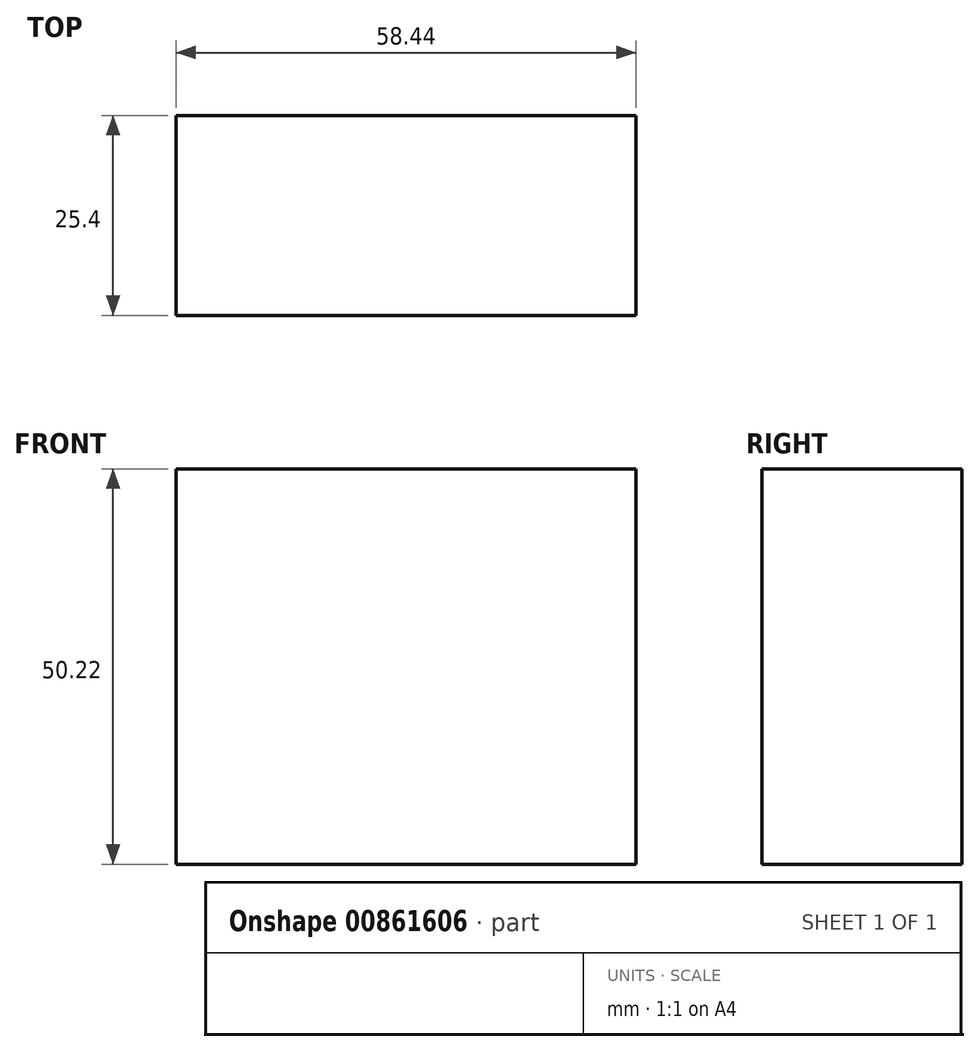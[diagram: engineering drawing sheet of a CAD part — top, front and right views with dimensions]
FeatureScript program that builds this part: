
annotation { "Feature Type Name" : "Feature", "Feature Type Description" : "" }
export const myFeature = defineFeature(function(context is Context, id is Id, definition is map)
    precondition{}
    {
        {
            var Q0;
            Q0=qCreatedBy(makeId("Front.planeOp"),FACE);
            var sketch = newSketch(context, id + "F0", { "sketchPlane" : qUnion([Q0])});
            skLineSegment(sketch, "E0.bottom", {"start": v(-29.22, 25.11) * mm, "end": v(29.22, 25.11) * mm});
            skLineSegment(sketch, "E0.top", {"start": v(-29.22, -25.11) * mm, "end": v(29.22, -25.11) * mm});
            skLineSegment(sketch, "E0.left", {"start": v(-29.22, 25.11) * mm, "end": v(-29.22, -25.11) * mm});
            skLineSegment(sketch, "E0.right", {"start": v(29.22, 25.11) * mm, "end": v(29.22, -25.11) * mm});
            skPoint(sketch, "E0.middle", {"position": v(0, 0) * mm});
            skSolve(sketch);
        }
        {
            var Q0;
            Q0=makeQuery(id+"F0.imprint","IMPRINT",FACE,{"disambiguationData":[TD([[makeQuery(id+"F0.imprint","IMPRINT",EDGE,{"derivedFrom":sQuery(id+"F0.wireOp",EDGE,"E0.bottom")}),-1.0]])]});
            extrude(context, id + "F1", {"entities" : qUnion([Q0]), "depth" : 25.4 * mm, "offsetDistance" : 25.4 * mm});
        }
    });
